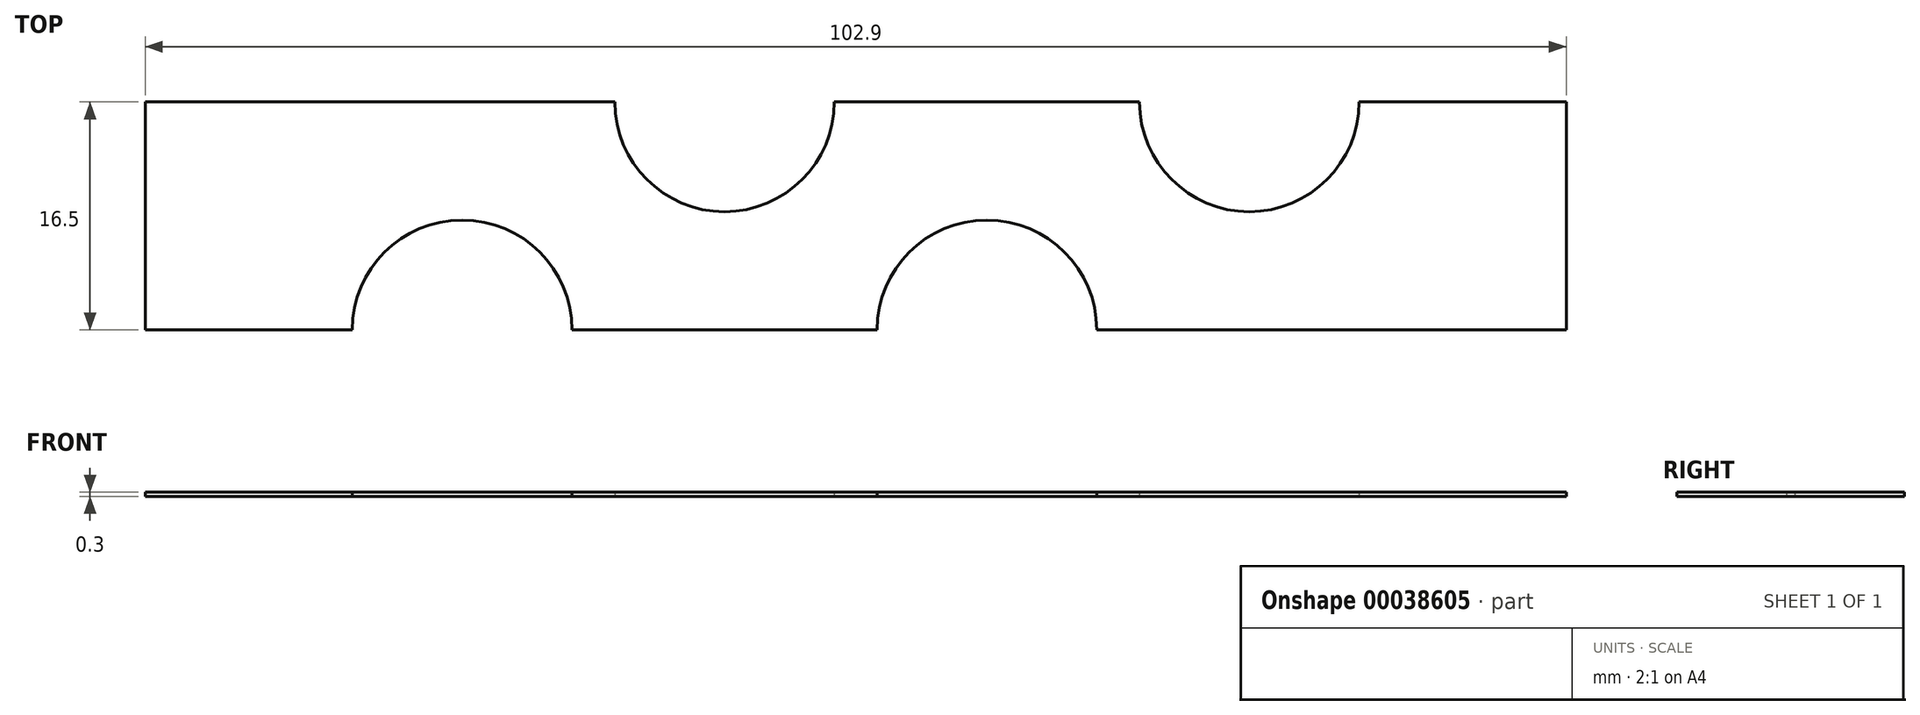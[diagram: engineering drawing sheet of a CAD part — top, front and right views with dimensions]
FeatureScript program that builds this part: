
annotation { "Feature Type Name" : "Feature", "Feature Type Description" : "" }
export const myFeature = defineFeature(function(context is Context, id is Id, definition is map)
    precondition{}
    {
        {
            var Q0;
            Q0=qCreatedBy(makeId("Top.planeOp"),FACE);
            var sketch = newSketch(context, id + "F0", { "sketchPlane" : qUnion([Q0])});
            skLineSegment(sketch, "E0.bottom", {"start": v(0, -8.25) * mm, "end": v(102.9, -8.25) * mm});
            skLineSegment(sketch, "E0.top", {"start": v(0, 8.25) * mm, "end": v(102.9, 8.25) * mm});
            skLineSegment(sketch, "E0.left", {"start": v(0, -8.25) * mm, "end": v(0, 8.25) * mm});
            skLineSegment(sketch, "E0.right", {"start": v(102.9, -8.25) * mm, "end": v(102.9, 8.25) * mm});
            skCircle(sketch, "E1", {"center": v(22.95, -8.25) * mm, "radius": 7.95 * mm});
            skCircle(sketch, "E2", {"center": v(41.95, 8.25) * mm, "radius": 7.95 * mm});
            skCircle(sketch, "E3", {"center": v(60.95, -8.25) * mm, "radius": 7.95 * mm});
            skCircle(sketch, "E4", {"center": v(79.95, 8.25) * mm, "radius": 7.95 * mm});
            skSolve(sketch);
        }
        {
            var Q0;
            {var subQ5=sQuery(id+"F0.wireOp",EDGE,"E0.left");Q0=makeQuery(id+"F0.imprint","IMPRINT",FACE,{"disambiguationData":[TD([[makeQuery(id+"F0.imprint","IMPRINT",EDGE,{"derivedFrom":subQ5}),-1.0]])]});}
            extrude(context, id + "F1", {"entities" : qUnion([Q0]), "depth" : 0.3 * mm});
        }
    });
